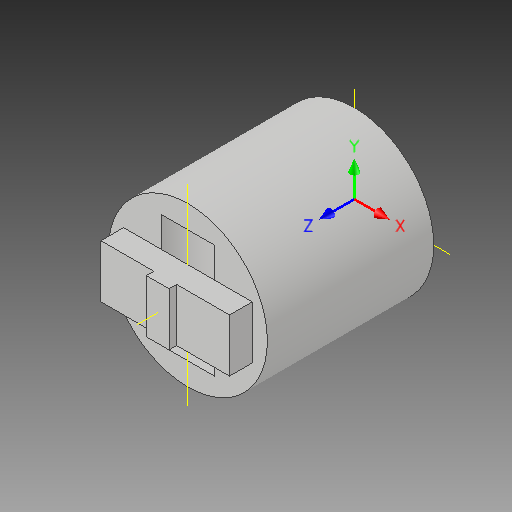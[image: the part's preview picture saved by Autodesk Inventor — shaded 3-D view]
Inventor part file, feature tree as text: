
AUTODESK INVENTOR PART (.ipt)
format: ipt  version: 2019 (Build 230136000, 136)  size: 131,072 bytes
history: native  units: in
note: dims shown in document units (in); Inventor stores cm internally (conversion verified against a paired STEP export)
features: other x10, extrude x4, sketch x4
ambient origin geometry x4: Origin, YZ Plane, XZ Plane, XY Plane
bodies: Solid1 (feature_tree)
feature tree (18):
  extrude  "Extrusion1"  Depth=6.9291in TaperAngle=0.0deg
  extrude  "Extrusion2"  Depth=4.7244in TaperAngle=0.0deg
  extrude  "Extrusion3"  Depth=2.2047in
  extrude  "Extrusion4"  Depth=0.9449in
  other  "Work Point2"
  other  "Work Point3"
  other  "UCS1"
  sketch  "Sketch1"  dims[d0=6.6142in d1=6.9291in d2=0.0in]
  sketch  "Sketch2"  dims[d3=2.2047in d4=4.7244in d5=0.0in]
  sketch  "Sketch4"  dims[d7=2.2047in d8=0.6299in]
  sketch  "Sketch5"  dims[d9=0.9449in d10=0.0in d11=0.9449in d12=0.315in d13=0.0in d14=0.0in d15=0.0in d16=0.0in d17=0.0in d18=0.0in d19=0.0in]
  other  "UCS1: YZ Plane"
  other  "UCS1: XZ Plane"
  other  "UCS1: XY Plane"
  other  "UCS1: X Axis"
  other  "UCS1: Y Axis"
  other  "UCS1: Z Axis"
  other  "UCS1: Center Point"
